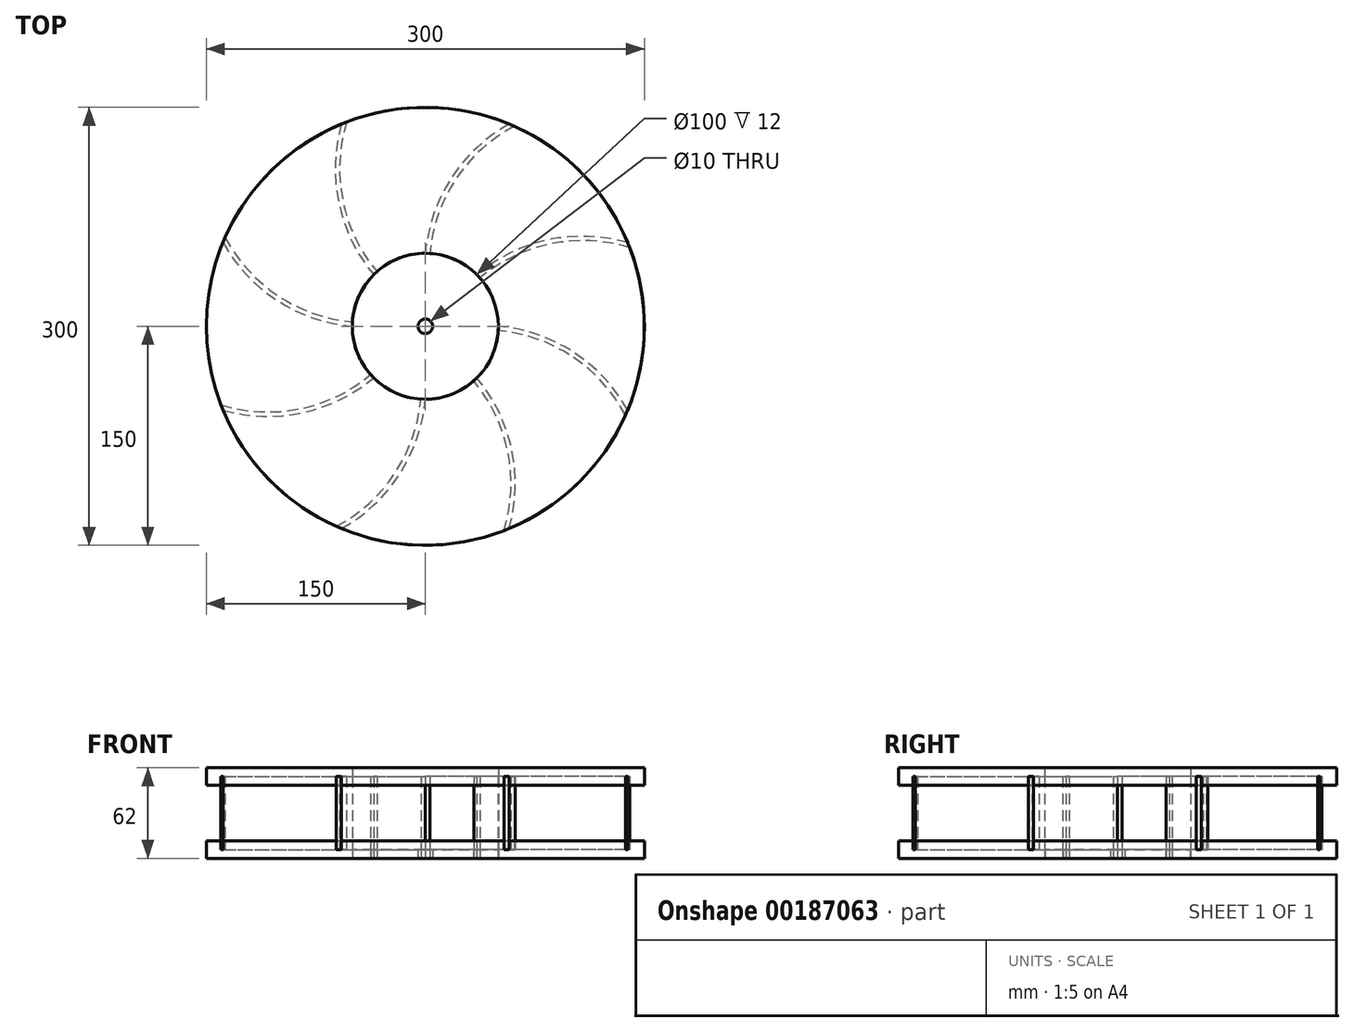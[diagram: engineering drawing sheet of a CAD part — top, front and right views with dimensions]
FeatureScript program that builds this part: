
annotation { "Feature Type Name" : "Feature", "Feature Type Description" : "" }
export const myFeature = defineFeature(function(context is Context, id is Id, definition is map)
    precondition{}
    {
        {
            assignVariable(context, id + "F0", {"name" : "RotorThickness", "anyValue" : 12});
        }
        {
            assignVariable(context, id + "F1", {"name" : "BladeDepth", "anyValue" : 50});
        }
        {
            var Q0;
            Q0=qCreatedBy(makeId("Top.planeOp"),FACE);
            var sketch = newSketch(context, id + "F2", { "sketchPlane" : qUnion([Q0])});
            skCircle(sketch, "E0", {"center": v(0, 0) * mm, "radius": 150 * mm});
            skCircle(sketch, "E1", {"center": v(0, 0) * mm, "radius": 50 * mm});
            skCircle(sketch, "E2", {"center": v(0, 0) * mm, "radius": 5 * mm});
            skLineSegment(sketch, "E3", {"start": v(0, 171.89) * mm, "end": v(0, -163.46) * mm, "construction": true});
            skLineSegment(sketch, "E4", {"start": v(67.03, 161.84) * mm, "end": v(-73.97, -178.58) * mm, "construction": true});
            skArc(sketch, "E5", {"start": v(57.4, 138.58) * mm, "mid": v(17.7, 101.42) * mm, "end": v(0, 50) * mm});
            skArc(sketch, "E6.0", {"start": v(60.91, 137.08) * mm, "mid": v(20.86, 100.76) * mm, "end": v(2.99, 49.74) * mm});
            skLineSegment(sketch, "E7", {"start": v(0, 50) * mm, "end": v(2.99, 49.74) * mm});
            skPoint(sketch, "E8", {"position": v(60.91, 137.08) * mm});
            skPoint(sketch, "E9", {"position": v(57.4, 138.58) * mm});
            skArc(sketch, "E10.1.0", {"start": v(-53.86, 140) * mm, "mid": v(-56.5, 86) * mm, "end": v(-33.06, 37.28) * mm});
            skArc(sketch, "E10.1.1", {"start": v(-57.4, 138.58) * mm, "mid": v(-59.2, 84.23) * mm, "end": v(-35.36, 35.36) * mm});
            skArc(sketch, "E10.2.0", {"start": v(-137.08, 60.91) * mm, "mid": v(-100.76, 20.86) * mm, "end": v(-49.74, 2.99) * mm});
            skArc(sketch, "E10.2.1", {"start": v(-138.58, 57.4) * mm, "mid": v(-101.42, 17.7) * mm, "end": v(-50, 0) * mm});
            skArc(sketch, "E10.3.0", {"start": v(-140, -53.86) * mm, "mid": v(-86, -56.5) * mm, "end": v(-37.28, -33.06) * mm});
            skArc(sketch, "E10.3.1", {"start": v(-138.58, -57.4) * mm, "mid": v(-84.23, -59.2) * mm, "end": v(-35.36, -35.36) * mm});
            skArc(sketch, "E10.4.0", {"start": v(-60.91, -137.08) * mm, "mid": v(-20.86, -100.76) * mm, "end": v(-2.99, -49.74) * mm});
            skArc(sketch, "E10.4.1", {"start": v(-57.4, -138.58) * mm, "mid": v(-17.7, -101.42) * mm, "end": v(0, -50) * mm});
            skArc(sketch, "E10.5.0", {"start": v(53.86, -140) * mm, "mid": v(56.5, -86) * mm, "end": v(33.06, -37.28) * mm});
            skArc(sketch, "E10.5.1", {"start": v(57.4, -138.58) * mm, "mid": v(59.2, -84.23) * mm, "end": v(35.36, -35.36) * mm});
            skArc(sketch, "E10.6.0", {"start": v(137.08, -60.91) * mm, "mid": v(100.76, -20.86) * mm, "end": v(49.74, -2.99) * mm});
            skArc(sketch, "E10.6.1", {"start": v(138.58, -57.4) * mm, "mid": v(101.42, -17.7) * mm, "end": v(50, 0) * mm});
            skArc(sketch, "E10.7.0", {"start": v(140, 53.86) * mm, "mid": v(86, 56.5) * mm, "end": v(37.28, 33.06) * mm});
            skArc(sketch, "E10.7.1", {"start": v(138.58, 57.4) * mm, "mid": v(84.23, 59.2) * mm, "end": v(35.36, 35.36) * mm});
            skLineSegment(sketch, "E11", {"start": v(-35.36, 35.36) * mm, "end": v(-33.06, 37.28) * mm});
            skLineSegment(sketch, "E12", {"start": v(-49.74, 2.99) * mm, "end": v(-50, 0) * mm});
            skLineSegment(sketch, "E13", {"start": v(35.36, 35.36) * mm, "end": v(37.28, 33.06) * mm});
            skLineSegment(sketch, "E14", {"start": v(50, 0) * mm, "end": v(49.74, -2.99) * mm});
            skLineSegment(sketch, "E15", {"start": v(35.36, -35.36) * mm, "end": v(33.06, -37.28) * mm});
            skLineSegment(sketch, "E16", {"start": v(0, -50) * mm, "end": v(-2.99, -49.74) * mm});
            skLineSegment(sketch, "E17", {"start": v(-35.36, -35.36) * mm, "end": v(-37.28, -33.06) * mm});
            skCircle(sketch, "E18", {"center": v(0, 0) * mm, "radius": 119.32 * mm, "construction": true});
            skSolve(sketch);
        }
        {
            var Q0;
            Q0 = qSketchRegion(id + "F2", true);
            var Q1;
            Q1=makeQuery(id+"F2.imprint","IMPRINT",FACE,{"disambiguationData":[TD([[makeQuery(id+"F2.imprint","IMPRINT",EDGE,{"derivedFrom":sQuery(id+"F2.wireOp",EDGE,"E2")}),-1.0]])]});
            extrude(context, id + "F3", {"entities" : qUnion([Q0, Q1]), "depth" : (getVariable(context, 'RotorThickness') * 0.5) * mm, "offsetDistance" : 25 * mm});
        }
        {
            var Q0;
            {var subQ0=sQuery(id+"F2.wireOp",EDGE,"E10.5.1");Q0=makeQuery(id+"F2.imprint","IMPRINT",FACE,{"disambiguationData":[TD([[makeQuery(id+"F2.imprint","IMPRINT",EDGE,{"derivedFrom":subQ0}),-1.0]])]});}
            var Q1;
            {var subQ0=sQuery(id+"F2.wireOp",EDGE,"E10.4.1");Q1=makeQuery(id+"F2.imprint","IMPRINT",FACE,{"disambiguationData":[TD([[makeQuery(id+"F2.imprint","IMPRINT",EDGE,{"derivedFrom":subQ0}),-1.0]])]});}
            var Q2;
            {var subQ0=sQuery(id+"F2.wireOp",EDGE,"E10.3.1");Q2=makeQuery(id+"F2.imprint","IMPRINT",FACE,{"disambiguationData":[TD([[makeQuery(id+"F2.imprint","IMPRINT",EDGE,{"derivedFrom":subQ0}),-1.0]])]});}
            var Q3;
            {var subQ0=sQuery(id+"F2.wireOp",EDGE,"E10.2.1");Q3=makeQuery(id+"F2.imprint","IMPRINT",FACE,{"disambiguationData":[TD([[makeQuery(id+"F2.imprint","IMPRINT",EDGE,{"derivedFrom":subQ0}),-1.0]])]});}
            var Q4;
            {var subQ0=sQuery(id+"F2.wireOp",EDGE,"E10.1.1");Q4=makeQuery(id+"F2.imprint","IMPRINT",FACE,{"disambiguationData":[TD([[makeQuery(id+"F2.imprint","IMPRINT",EDGE,{"derivedFrom":subQ0}),-1.0]])]});}
            var Q5;
            {var subQ0=sQuery(id+"F2.wireOp",EDGE,"E5");Q5=makeQuery(id+"F2.imprint","IMPRINT",FACE,{"disambiguationData":[TD([[makeQuery(id+"F2.imprint","IMPRINT",EDGE,{"derivedFrom":subQ0}),-1.0]])]});}
            var Q6;
            {var subQ3=sQuery(id+"F2.wireOp",EDGE,"E10.7.1");Q6=makeQuery(id+"F2.imprint","IMPRINT",FACE,{"disambiguationData":[TD([[makeQuery(id+"F2.imprint","IMPRINT",EDGE,{"derivedFrom":subQ3}),-1.0]])]});}
            var Q7;
            {var subQ0=sQuery(id+"F2.wireOp",EDGE,"E10.6.1");Q7=makeQuery(id+"F2.imprint","IMPRINT",FACE,{"disambiguationData":[TD([[makeQuery(id+"F2.imprint","IMPRINT",EDGE,{"derivedFrom":subQ0}),-1.0]])]});}
            extrude(context, id + "F4", {"entities" : qUnion([Q0, Q1, Q2, Q3, Q4, Q5, Q6, Q7]), "operationType" : NewBodyOperationType.ADD, "depth" : (getVariable(context, 'RotorThickness')) * mm, "hasSecondDirection" : true, "secondDirectionOppositeDirection" : false, "secondDirectionDepth" : (getVariable(context, 'RotorThickness') * 0.5) * mm, "offsetDistance" : 25 * mm});
        }
        {
            var Q0;
            Q0 = qSketchRegion(id + "F2", true);
            extrude(context, id + "F5", {"entities" : qUnion([Q0]), "operationType" : NewBodyOperationType.ADD, "depth" : (getVariable(context, 'BladeDepth') + getVariable(context, 'RotorThickness')) * mm, "hasSecondDirection" : true, "secondDirectionOppositeDirection" : false, "secondDirectionDepth" : (getVariable(context, 'BladeDepth') + getVariable(context, 'RotorThickness') * 0.5) * mm, "offsetDistance" : 25 * mm});
        }
        {
            var Q0;
            {var subQ0=sQuery(id+"F2.wireOp",EDGE,"E10.1.1");Q0=makeQuery(id+"F2.imprint","IMPRINT",FACE,{"disambiguationData":[TD([[makeQuery(id+"F2.imprint","IMPRINT",EDGE,{"derivedFrom":subQ0}),-1.0]])]});}
            var Q1;
            {var subQ0=sQuery(id+"F2.wireOp",EDGE,"E5");Q1=makeQuery(id+"F2.imprint","IMPRINT",FACE,{"disambiguationData":[TD([[makeQuery(id+"F2.imprint","IMPRINT",EDGE,{"derivedFrom":subQ0}),-1.0]])]});}
            var Q2;
            {var subQ3=sQuery(id+"F2.wireOp",EDGE,"E10.7.1");Q2=makeQuery(id+"F2.imprint","IMPRINT",FACE,{"disambiguationData":[TD([[makeQuery(id+"F2.imprint","IMPRINT",EDGE,{"derivedFrom":subQ3}),-1.0]])]});}
            var Q3;
            {var subQ0=sQuery(id+"F2.wireOp",EDGE,"E10.6.1");Q3=makeQuery(id+"F2.imprint","IMPRINT",FACE,{"disambiguationData":[TD([[makeQuery(id+"F2.imprint","IMPRINT",EDGE,{"derivedFrom":subQ0}),-1.0]])]});}
            var Q4;
            {var subQ0=sQuery(id+"F2.wireOp",EDGE,"E10.5.1");Q4=makeQuery(id+"F2.imprint","IMPRINT",FACE,{"disambiguationData":[TD([[makeQuery(id+"F2.imprint","IMPRINT",EDGE,{"derivedFrom":subQ0}),-1.0]])]});}
            var Q5;
            {var subQ0=sQuery(id+"F2.wireOp",EDGE,"E10.4.1");Q5=makeQuery(id+"F2.imprint","IMPRINT",FACE,{"disambiguationData":[TD([[makeQuery(id+"F2.imprint","IMPRINT",EDGE,{"derivedFrom":subQ0}),-1.0]])]});}
            var Q6;
            {var subQ0=sQuery(id+"F2.wireOp",EDGE,"E10.3.1");Q6=makeQuery(id+"F2.imprint","IMPRINT",FACE,{"disambiguationData":[TD([[makeQuery(id+"F2.imprint","IMPRINT",EDGE,{"derivedFrom":subQ0}),-1.0]])]});}
            var Q7;
            {var subQ0=sQuery(id+"F2.wireOp",EDGE,"E10.2.1");Q7=makeQuery(id+"F2.imprint","IMPRINT",FACE,{"disambiguationData":[TD([[makeQuery(id+"F2.imprint","IMPRINT",EDGE,{"derivedFrom":subQ0}),-1.0]])]});}
            extrude(context, id + "F6", {"entities" : qUnion([Q0, Q1, Q2, Q3, Q4, Q5, Q6, Q7]), "operationType" : NewBodyOperationType.ADD, "depth" : (getVariable(context, 'BladeDepth') + getVariable(context, 'RotorThickness')) * mm, "hasSecondDirection" : true, "secondDirectionOppositeDirection" : false, "secondDirectionDepth" : (getVariable(context, 'BladeDepth')) * mm, "offsetDistance" : 25 * mm});
        }
        {
            var Q0;
            {var subQ3=sQuery(id+"F2.wireOp",EDGE,"E10.1.1");Q0=makeQuery(id+"F2.imprint","IMPRINT",FACE,{"disambiguationData":[TD([[makeQuery(id+"F2.imprint","IMPRINT",EDGE,{"derivedFrom":subQ3}),1.0]])]});}
            var Q1;
            {var subQ0=sQuery(id+"F2.wireOp",EDGE,"E5");Q1=makeQuery(id+"F2.imprint","IMPRINT",FACE,{"disambiguationData":[TD([[makeQuery(id+"F2.imprint","IMPRINT",EDGE,{"derivedFrom":subQ0}),1.0]])]});}
            var Q2;
            {var subQ3=sQuery(id+"F2.wireOp",EDGE,"E10.2.1");Q2=makeQuery(id+"F2.imprint","IMPRINT",FACE,{"disambiguationData":[TD([[makeQuery(id+"F2.imprint","IMPRINT",EDGE,{"derivedFrom":subQ3}),1.0]])]});}
            var Q3;
            {var subQ3=sQuery(id+"F2.wireOp",EDGE,"E10.7.1");Q3=makeQuery(id+"F2.imprint","IMPRINT",FACE,{"disambiguationData":[TD([[makeQuery(id+"F2.imprint","IMPRINT",EDGE,{"derivedFrom":subQ3}),1.0]])]});}
            var Q4;
            {var subQ3=sQuery(id+"F2.wireOp",EDGE,"E10.6.1");Q4=makeQuery(id+"F2.imprint","IMPRINT",FACE,{"disambiguationData":[TD([[makeQuery(id+"F2.imprint","IMPRINT",EDGE,{"derivedFrom":subQ3}),1.0]])]});}
            var Q5;
            {var subQ3=sQuery(id+"F2.wireOp",EDGE,"E10.5.1");Q5=makeQuery(id+"F2.imprint","IMPRINT",FACE,{"disambiguationData":[TD([[makeQuery(id+"F2.imprint","IMPRINT",EDGE,{"derivedFrom":subQ3}),1.0]])]});}
            var Q6;
            {var subQ3=sQuery(id+"F2.wireOp",EDGE,"E10.4.1");Q6=makeQuery(id+"F2.imprint","IMPRINT",FACE,{"disambiguationData":[TD([[makeQuery(id+"F2.imprint","IMPRINT",EDGE,{"derivedFrom":subQ3}),1.0]])]});}
            var Q7;
            {var subQ3=sQuery(id+"F2.wireOp",EDGE,"E10.3.1");Q7=makeQuery(id+"F2.imprint","IMPRINT",FACE,{"disambiguationData":[TD([[makeQuery(id+"F2.imprint","IMPRINT",EDGE,{"derivedFrom":subQ3}),1.0]])]});}
            extrude(context, id + "F7", {"entities" : qUnion([Q0, Q1, Q2, Q3, Q4, Q5, Q6, Q7]), "depth" : (getVariable(context, 'BladeDepth') + getVariable(context, 'RotorThickness') * 0.5) * mm, "offsetDistance" : 25 * mm, "hasSecondDirection" : true, "secondDirectionOppositeDirection" : false, "secondDirectionDepth" : (getVariable(context, 'RotorThickness') * 0.5) * mm});
        }
    });
